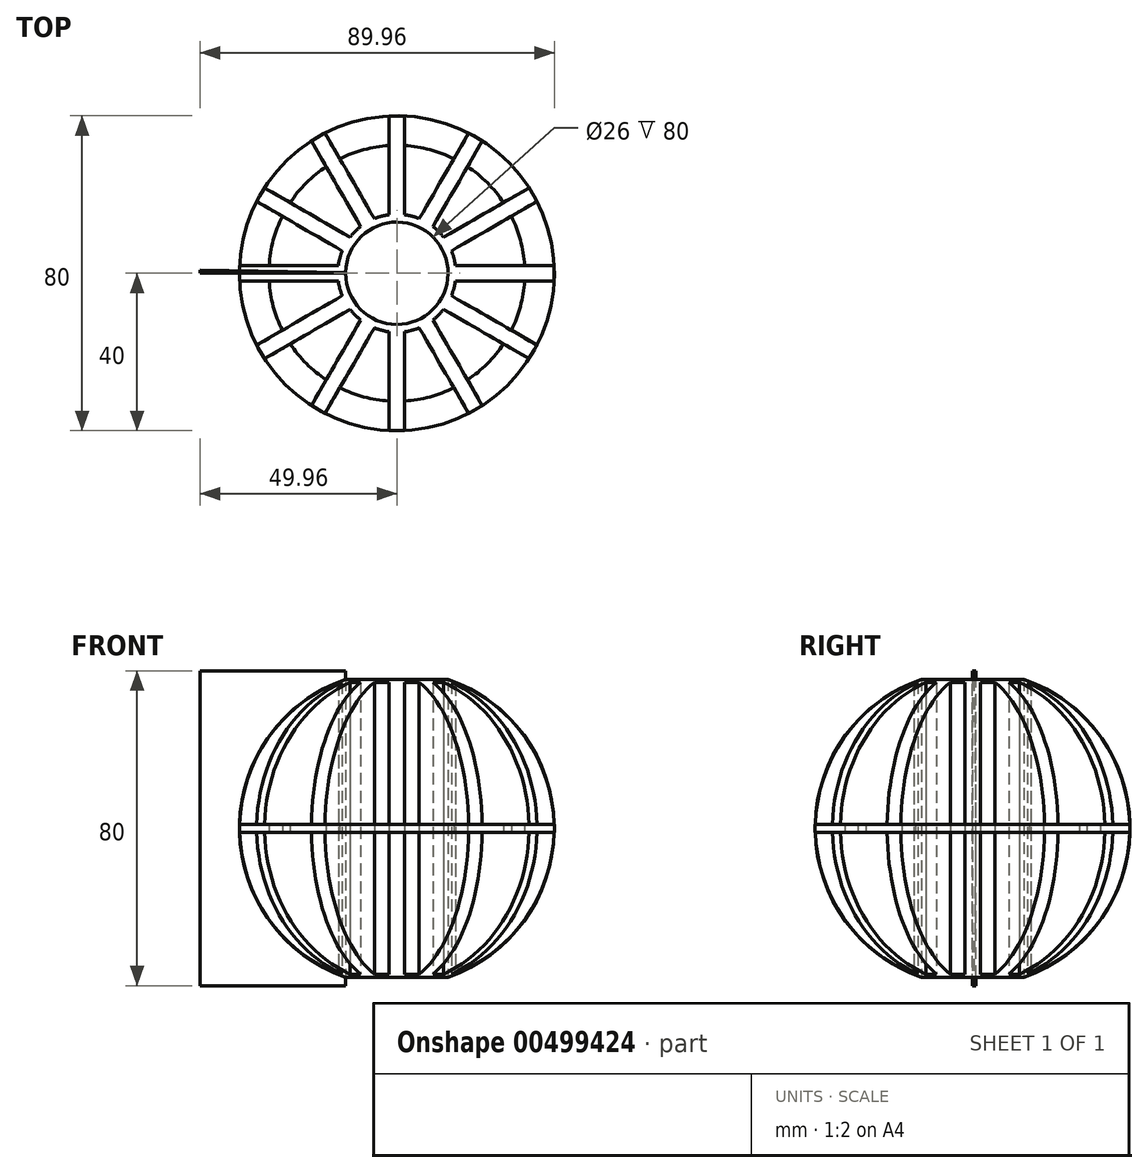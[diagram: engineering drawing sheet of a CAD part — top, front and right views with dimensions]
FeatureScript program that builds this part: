
annotation { "Feature Type Name" : "Feature", "Feature Type Description" : "" }
export const myFeature = defineFeature(function(context is Context, id is Id, definition is map)
    precondition{}
    {
        {
            var Q0;
            Q0=qCreatedBy(makeId("Top.planeOp"),FACE);
            var sketch = newSketch(context, id + "F0", { "sketchPlane" : qUnion([Q0])});
            skCircle(sketch, "E0", {"center": v(0, 0) * mm, "radius": 15 * mm});
            skArc(sketch, "E1", {"start": v(2, 49.96) * mm, "mid": v(0, 50) * mm, "end": v(-2, 49.96) * mm, "construction": true});
            skCircle(sketch, "E2", {"center": v(0, 0) * mm, "radius": 13 * mm});
            skLineSegment(sketch, "E3", {"start": v(-2, 49.96) * mm, "end": v(-2, 12.85) * mm});
            skLineSegment(sketch, "E4", {"start": v(2, 49.96) * mm, "end": v(2, 12.85) * mm});
            skLineSegment(sketch, "E5", {"start": v(-2, 49.96) * mm, "end": v(2, 49.96) * mm});
            skLineSegment(sketch, "E6.1.0", {"start": v(-26.71, 42.27) * mm, "end": v(-8.15, 10.12) * mm});
            skLineSegment(sketch, "E6.1.1", {"start": v(-23.25, 44.27) * mm, "end": v(-4.7, 12.12) * mm});
            skArc(sketch, "E6.1.2", {"start": v(-23.25, 44.27) * mm, "mid": v(-25, 43.3) * mm, "end": v(-26.71, 42.27) * mm, "construction": true});
            skLineSegment(sketch, "E6.2.0", {"start": v(-44.27, 23.25) * mm, "end": v(-12.12, 4.7) * mm});
            skLineSegment(sketch, "E6.2.1", {"start": v(-42.27, 26.71) * mm, "end": v(-10.12, 8.15) * mm});
            skArc(sketch, "E6.2.2", {"start": v(-42.27, 26.71) * mm, "mid": v(-43.3, 25) * mm, "end": v(-44.27, 23.25) * mm, "construction": true});
            skLineSegment(sketch, "E6.3.0", {"start": v(-49.96, -2) * mm, "end": v(-12.85, -2) * mm});
            skLineSegment(sketch, "E6.3.1", {"start": v(-49.96, 2) * mm, "end": v(-12.85, 2) * mm});
            skArc(sketch, "E6.3.2", {"start": v(-49.96, 2) * mm, "mid": v(-50, 0) * mm, "end": v(-49.96, -2) * mm, "construction": true});
            skLineSegment(sketch, "E6.4.0", {"start": v(-42.27, -26.71) * mm, "end": v(-10.12, -8.15) * mm});
            skLineSegment(sketch, "E6.4.1", {"start": v(-44.27, -23.25) * mm, "end": v(-12.12, -4.7) * mm});
            skArc(sketch, "E6.4.2", {"start": v(-44.27, -23.25) * mm, "mid": v(-43.3, -25) * mm, "end": v(-42.27, -26.71) * mm, "construction": true});
            skLineSegment(sketch, "E6.5.0", {"start": v(-23.25, -44.27) * mm, "end": v(-4.7, -12.12) * mm});
            skLineSegment(sketch, "E6.5.1", {"start": v(-26.71, -42.27) * mm, "end": v(-8.15, -10.12) * mm});
            skArc(sketch, "E6.5.2", {"start": v(-26.71, -42.27) * mm, "mid": v(-25, -43.3) * mm, "end": v(-23.25, -44.27) * mm, "construction": true});
            skLineSegment(sketch, "E6.6.0", {"start": v(2, -49.96) * mm, "end": v(2, -12.85) * mm});
            skLineSegment(sketch, "E6.6.1", {"start": v(-2, -49.96) * mm, "end": v(-2, -12.85) * mm});
            skArc(sketch, "E6.6.2", {"start": v(-2, -49.96) * mm, "mid": v(0, -50) * mm, "end": v(2, -49.96) * mm, "construction": true});
            skLineSegment(sketch, "E6.7.0", {"start": v(26.71, -42.27) * mm, "end": v(8.15, -10.12) * mm});
            skLineSegment(sketch, "E6.7.1", {"start": v(23.25, -44.27) * mm, "end": v(4.7, -12.12) * mm});
            skArc(sketch, "E6.7.2", {"start": v(23.25, -44.27) * mm, "mid": v(25, -43.3) * mm, "end": v(26.71, -42.27) * mm, "construction": true});
            skLineSegment(sketch, "E6.8.0", {"start": v(44.27, -23.25) * mm, "end": v(12.12, -4.7) * mm});
            skLineSegment(sketch, "E6.8.1", {"start": v(42.27, -26.71) * mm, "end": v(10.12, -8.15) * mm});
            skArc(sketch, "E6.8.2", {"start": v(42.27, -26.71) * mm, "mid": v(43.3, -25) * mm, "end": v(44.27, -23.25) * mm, "construction": true});
            skLineSegment(sketch, "E6.9.0", {"start": v(49.96, 2) * mm, "end": v(12.85, 2) * mm});
            skLineSegment(sketch, "E6.9.1", {"start": v(49.96, -2) * mm, "end": v(12.85, -2) * mm});
            skArc(sketch, "E6.9.2", {"start": v(49.96, -2) * mm, "mid": v(50, 0) * mm, "end": v(49.96, 2) * mm, "construction": true});
            skLineSegment(sketch, "E6.10.0", {"start": v(42.27, 26.71) * mm, "end": v(10.12, 8.15) * mm});
            skLineSegment(sketch, "E6.10.1", {"start": v(44.27, 23.25) * mm, "end": v(12.12, 4.7) * mm});
            skArc(sketch, "E6.10.2", {"start": v(44.27, 23.25) * mm, "mid": v(43.3, 25) * mm, "end": v(42.27, 26.71) * mm, "construction": true});
            skLineSegment(sketch, "E6.11.0", {"start": v(23.25, 44.27) * mm, "end": v(4.7, 12.12) * mm});
            skLineSegment(sketch, "E6.11.1", {"start": v(26.71, 42.27) * mm, "end": v(8.15, 10.12) * mm});
            skArc(sketch, "E6.11.2", {"start": v(26.71, 42.27) * mm, "mid": v(25, 43.3) * mm, "end": v(23.25, 44.27) * mm, "construction": true});
            skLineSegment(sketch, "E7", {"start": v(-26.71, 42.27) * mm, "end": v(-23.25, 44.27) * mm});
            skLineSegment(sketch, "E8", {"start": v(23.25, 44.27) * mm, "end": v(26.71, 42.27) * mm});
            skLineSegment(sketch, "E9", {"start": v(42.27, 26.71) * mm, "end": v(44.27, 23.25) * mm});
            skLineSegment(sketch, "E10", {"start": v(49.96, 2) * mm, "end": v(49.96, -2) * mm});
            skLineSegment(sketch, "E11", {"start": v(44.27, -23.25) * mm, "end": v(42.27, -26.71) * mm});
            skLineSegment(sketch, "E12", {"start": v(26.71, -42.27) * mm, "end": v(23.25, -44.27) * mm});
            skLineSegment(sketch, "E13", {"start": v(2, -49.96) * mm, "end": v(-2, -49.96) * mm});
            skLineSegment(sketch, "E14", {"start": v(-23.25, -44.27) * mm, "end": v(-26.71, -42.27) * mm});
            skLineSegment(sketch, "E15", {"start": v(-42.27, -26.71) * mm, "end": v(-44.27, -23.25) * mm});
            skLineSegment(sketch, "E16", {"start": v(-49.96, -2) * mm, "end": v(-49.96, 2) * mm});
            skLineSegment(sketch, "E17", {"start": v(-44.27, 23.25) * mm, "end": v(-42.27, 26.71) * mm});
            skSolve(sketch);
        }
        {
            var Q0;
            Q0 = qSketchRegion(id + "F0", true);
            extrude(context, id + "F1", {"entities" : qUnion([Q0]), "endBound" : BoundingType.SYMMETRIC, "depth" : 80 * mm});
        }
        {
            var Q0;
            Q0=qCreatedBy(makeId("Front.planeOp"),FACE);
            var sketch = newSketch(context, id + "F2", { "sketchPlane" : qUnion([Q0])});
            skArc(sketch, "E18", {"start": v(0, 40) * mm, "mid": v(-40, 0) * mm, "end": v(0, -40) * mm});
            skLineSegment(sketch, "E19", {"start": v(0, 40) * mm, "end": v(-50, 40) * mm});
            skLineSegment(sketch, "E20", {"start": v(-50, 40) * mm, "end": v(-50, -40) * mm});
            skLineSegment(sketch, "E21", {"start": v(-50, -40) * mm, "end": v(0, -40) * mm});
            skPoint(sketch, "E22.orphan", {"position": v(0, 53.88) * mm});
            skLineSegment(sketch, "E23", {"start": v(0, -65.2) * mm, "end": v(0, 53.88) * mm, "construction": true});
            skSolve(sketch);
        }
        {
            var Q0;
            Q0 = qSketchRegion(id + "F2", true);
            var Q1;
            Q1=makeQuery(id+"F1.opExtrude","CAP_EDGE",EDGE,{"disambiguationData":[OSD([sQuery(id+"F0.wireOp",EDGE,"E2")])],"isStart":true});
            revolve(context, id + "F3", {"operationType" : NewBodyOperationType.REMOVE, "entities" : qUnion([Q0]), "axis" : qUnion([Q1]), "revolveType" : RevolveType.ONE_DIRECTION, "angle" : 359 * degree});
        }
        {
            var Q0;
            Q0=qCreatedBy(makeId("Top.planeOp"),FACE);
            var sketch = newSketch(context, id + "F4", { "sketchPlane" : qUnion([Q0])});
            skCircle(sketch, "E24", {"center": v(0, 0) * mm, "radius": 40 * mm});
            skCircle(sketch, "E25", {"center": v(0, 0) * mm, "radius": 32.5 * mm});
            skCircle(sketch, "E26", {"center": v(0, 0) * mm, "radius": 30 * mm});
            skCircle(sketch, "E27", {"center": v(0, 0) * mm, "radius": 17.5 * mm});
            skSolve(sketch);
        }
        {
            var Q0;
            Q0 = qSketchRegion(id + "F4", true);
            extrude(context, id + "F5", {"entities" : qUnion([Q0]), "operationType" : NewBodyOperationType.ADD, "endBound" : BoundingType.SYMMETRIC, "depth" : 2 * mm});
        }
    });
